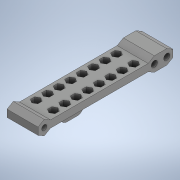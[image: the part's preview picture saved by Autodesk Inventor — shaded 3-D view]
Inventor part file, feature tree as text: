
AUTODESK INVENTOR PART (.ipt)
format: ipt  version: 2020 (Build 240168000, 168)  size: 470,016 bytes
history: native  units: in
note: dims shown in document units (in); Inventor stores cm internally (conversion verified against a paired STEP export)
features: sketch x7, extrude x6, projected_geometry x4, plane x2, mirror x1, fillet x1
ambient origin geometry x8: Origin, YZ Plane, XZ Plane, XY Plane, X Axis, Y Axis, Z Axis, Center Point
bodies: Solid1 (feature_tree)
feature tree (21):
  extrude  "Extrusion1"  Depth=3.4256in
  plane  "Work Plane1"
  extrude  "Extrusion2"  Depth=0.7874in
  sketch  "Sketch4"  dims[d4=0.0in d5=0.0827in]
  extrude  "Extrusion4"  Depth=0.0827in
  plane  "Work Plane2"
  extrude  "Extrusion6"  Depth=3.1106in
  mirror  "Mirror2"
  extrude  "Extrusion7"  Depth=0.315in
  extrude  "Extrusion8"  Depth=0.2362in
  fillet  "Fillet1"  [1 undecoded]
  sketch  "Sketch1"  dims[d0=0.1818in d1=3.4256in]
  sketch  "Sketch2"  dims[d2=0.1339in d3=0.7874in]
  sketch  "Sketch5"  dims[d6=0.7874in d7=0.0in d28=3.1106in]
  sketch  "Sketch7"  dims[d29=0.315in d31=0.315in]
  projected_geometry  "Projected Loop7"
  projected_geometry  "Projected Loop8"
  sketch  "Sketch8"  dims[d33=0.1575in d34=0.2362in d35=0.0in]
  projected_geometry  "Projected Loop9"
  sketch  "Sketch10"  dims[d38=0.315in d39=0.2756in d40=-0.3092in d41=0.0787in d42=0.0787in d43=0.0787in d44=3.1496in d46=0.2913in d47=0.3937in d49=0.3937in d51=3.1496in d53=0.2913in d54=0.3937in d56=0.3937in d58=0.0in d59=0.0in d60=150.0deg d61=0.1339in d63=1.1811in d64=0.1575in d65=0.0in d66=0.126in d67=0.1575in]
  projected_geometry  "Projected Loop10"
note: 1 required parameter value undecoded (feature->parameter linkage not recoverable at this tier; creation-order binding heuristic only, values carry confidence <= 0.55)
